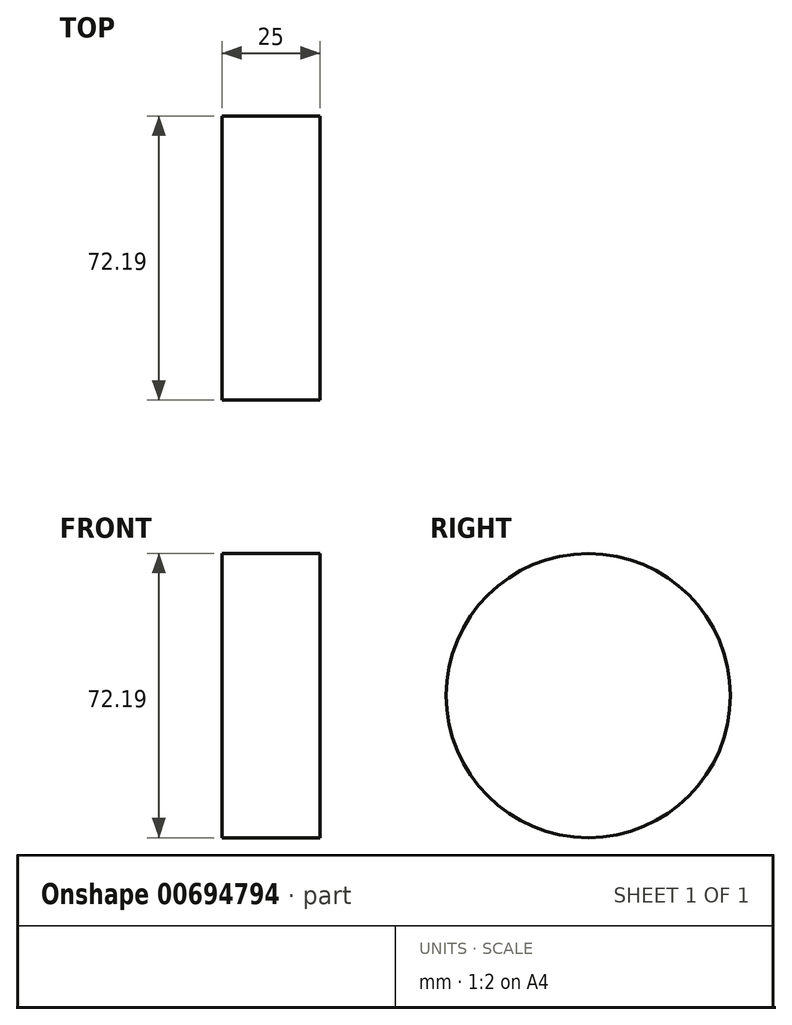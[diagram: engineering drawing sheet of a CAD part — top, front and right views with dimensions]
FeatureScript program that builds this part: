
annotation { "Feature Type Name" : "Feature", "Feature Type Description" : "" }
export const myFeature = defineFeature(function(context is Context, id is Id, definition is map)
    precondition{}
    {
        {
            var Q0;
            Q0=qCreatedBy(makeId("Right.planeOp"),FACE);
            var sketch = newSketch(context, id + "F0", { "sketchPlane" : qUnion([Q0])});
            skCircle(sketch, "E0", {"center": v(-37.1, 30.48) * mm, "radius": 36.1 * mm});
            skSolve(sketch);
        }
        {
            var Q0;
            Q0=makeQuery(id+"F0.imprint","IMPRINT",FACE,{"disambiguationData":[TD([[makeQuery(id+"F0.imprint","IMPRINT",EDGE,{"derivedFrom":sQuery(id+"F0.wireOp",EDGE,"E0")}),1.0]])]});
            extrude(context, id + "F1", {"entities" : qUnion([Q0]), "depth" : 25 * mm});
        }
    });
